# Revit family: AXOR_39410XXX-AXOR-Citterio-Bath-spout_1
name_source: partatom
category: Plumbing Fixtures
revit_build: Autodesk Revit 2015 (Build: 20140322_1515(x64)
units: mm (PartAtom-declared; Revit-internal decimal feet)

## types (16) — shared parameters
Brand url = https://www.axor-design.com
Default Elevation = 1219.2 mm  [stored 4 ft]
Design country = Germany
Edition number = 1
GTIN code = https://4011097400761
IFC Classification = Sanitary Terminal
Installation instructions = https://www.axor-design.com
Manufacturer country = Germany
Manufacturer name = AXOR
Material main = Chrome
Product Guid = cc02be90-9125-4cd8-bf5a-d358199b4ec6
Product SKU = 39410XXX
Product data url = https://bimobject.com
Product family = AXOR Citterio
Product group = Bath fillers
Product name = 39410XXX AXOR Citterio Bath spout
Product url = https://www.axor-design.com
QR code = http://bimobject.com
Technical description = https://www.axor-design.com

## type names (no varying parameters)
- 000 Chrome
- 020 Polished Chrome
- 130 Polished Bronze
- 140 Brushed Bronze
- 250 Brushed Gold Optic
- 260 Brushed Chrome
- 300 Polished Red Gold
- 310 Brushed Red Gold
- 330 Polished Black Chrome
- 340 Brushed Black Chrome
- 800 Stainless Steel Optic
- 820 Brushed Nickel
- 830 Polished Nickel
- 950 Brushed Brass
- 930 Polished Brass
- 990 Polished Gold Optic

note: [stored X ft] marks values corroborated as IEEE doubles in the binary element streams (Revit-internal decimal feet)

## geometry (parser evidence)
native form markers: Sweep x3
no freeform markers — native parametric forms only
